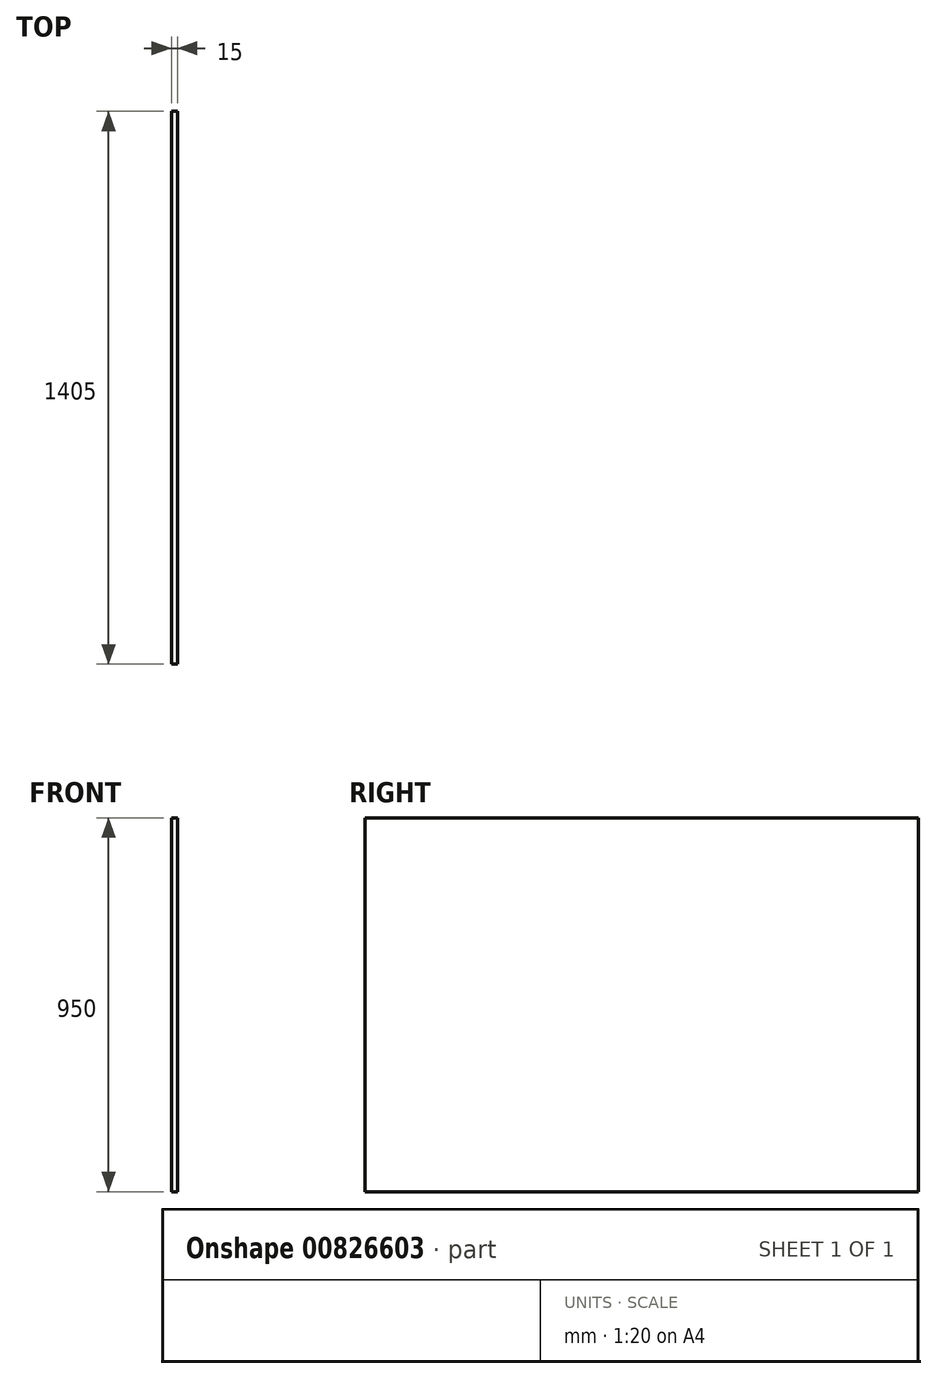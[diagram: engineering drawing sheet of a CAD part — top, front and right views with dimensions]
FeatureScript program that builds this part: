
annotation { "Feature Type Name" : "Feature", "Feature Type Description" : "" }
export const myFeature = defineFeature(function(context is Context, id is Id, definition is map)
    precondition{}
    {
        {
            var Q0;
            Q0=qCreatedBy(makeId("Right.planeOp"),FACE);
            var sketch = newSketch(context, id + "F0", { "sketchPlane" : qUnion([Q0])});
            skLineSegment(sketch, "E0.bottom", {"start": v(-694.86, 330.64) * mm, "end": v(710.14, 330.64) * mm});
            skLineSegment(sketch, "E0.top", {"start": v(-694.86, -619.36) * mm, "end": v(710.14, -619.36) * mm});
            skLineSegment(sketch, "E0.left", {"start": v(-694.86, 330.64) * mm, "end": v(-694.86, -619.36) * mm});
            skLineSegment(sketch, "E0.right", {"start": v(710.14, 330.64) * mm, "end": v(710.14, -619.36) * mm});
            skLineSegment(sketch, "E1.bottom", {"start": v(-4.5, 605.77) * mm, "end": v(-19.1, 605.77) * mm});
            skLineSegment(sketch, "E1.top", {"start": v(-4.5, 591.18) * mm, "end": v(-19.1, 591.18) * mm});
            skLineSegment(sketch, "E1.left", {"start": v(-4.5, 605.77) * mm, "end": v(-4.5, 591.18) * mm});
            skLineSegment(sketch, "E1.right", {"start": v(-19.1, 605.77) * mm, "end": v(-19.1, 591.18) * mm});
            skSolve(sketch);
        }
        {
            var Q0;
            Q0=makeQuery(id+"F0.imprint","IMPRINT",FACE,{"disambiguationData":[TD([[makeQuery(id+"F0.imprint","IMPRINT",EDGE,{"derivedFrom":sQuery(id+"F0.wireOp",EDGE,"E0.bottom")}),-1.0]])]});
            extrude(context, id + "F1", {"entities" : qUnion([Q0]), "depth" : 15 * mm, "offsetDistance" : 25 * mm});
        }
    });
